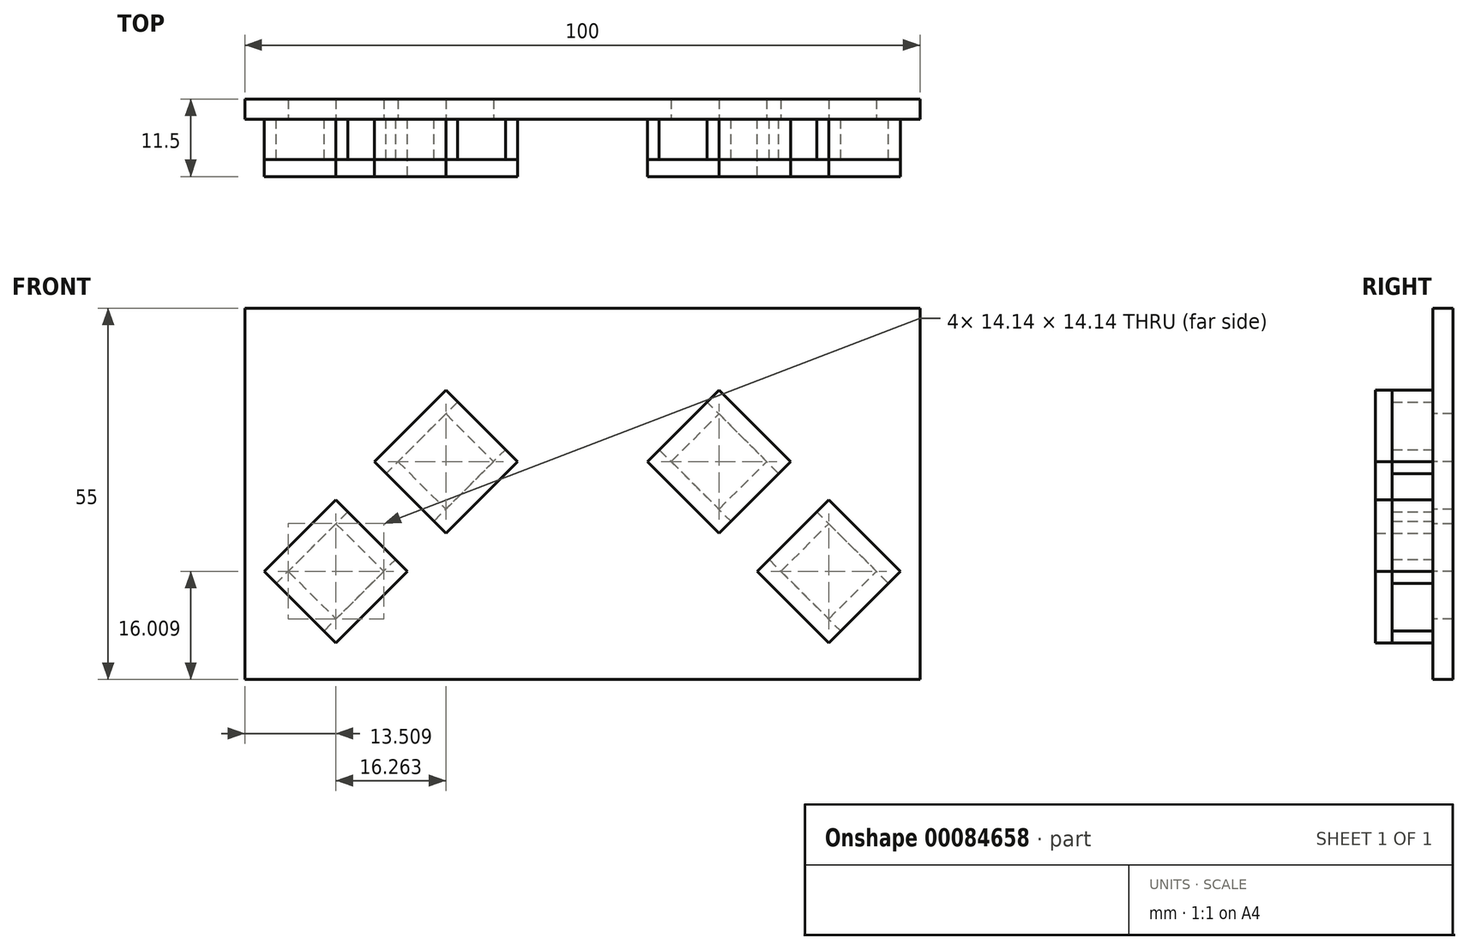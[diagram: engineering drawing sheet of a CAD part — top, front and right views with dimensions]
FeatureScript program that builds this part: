
annotation { "Feature Type Name" : "Feature", "Feature Type Description" : "" }
export const myFeature = defineFeature(function(context is Context, id is Id, definition is map)
    precondition{}
    {
        {
            var Q0;
            Q0=qCreatedBy(makeId("Front.planeOp"),FACE);
            var sketch = newSketch(context, id + "F0", { "sketchPlane" : qUnion([Q0])});
            skLineSegment(sketch, "E0.top", {"start": v(50, -45) * mm, "end": v(-50, -45) * mm});
            skLineSegment(sketch, "E0.left", {"start": v(50, 0) * mm, "end": v(50, -45) * mm});
            skLineSegment(sketch, "E0.right", {"start": v(-50, 0) * mm, "end": v(-50, -45) * mm});
            skPoint(sketch, "E0.middle", {"position": v(0, 0) * mm});
            skLineSegment(sketch, "E1", {"start": v(0, 0) * mm, "end": v(0, -45) * mm});
            skLineSegment(sketch, "E2", {"start": v(-50, 0) * mm, "end": v(50, 0) * mm});
            skLineSegment(sketch, "E3.0", {"start": v(13.16, -12.73) * mm, "end": v(20.23, -19.8) * mm});
            skLineSegment(sketch, "E4.0", {"start": v(20.23, -5.66) * mm, "end": v(27.3, -12.73) * mm});
            skLineSegment(sketch, "E5.0", {"start": v(-20.23, -5.66) * mm, "end": v(-13.16, -12.73) * mm});
            skLineSegment(sketch, "E6.0", {"start": v(13.16, -12.73) * mm, "end": v(20.23, -5.66) * mm});
            skLineSegment(sketch, "E7.0", {"start": v(-27.3, -12.73) * mm, "end": v(-20.23, -19.8) * mm});
            skLineSegment(sketch, "E8.0", {"start": v(20.23, -19.8) * mm, "end": v(27.3, -12.73) * mm});
            skLineSegment(sketch, "E9.0", {"start": v(-36.5, -21.92) * mm, "end": v(-29.42, -29) * mm});
            skLineSegment(sketch, "E10.0", {"start": v(29.42, -29) * mm, "end": v(36.5, -21.92) * mm});
            skLineSegment(sketch, "E11.0", {"start": v(-43.56, -29) * mm, "end": v(-36.5, -36.06) * mm});
            skLineSegment(sketch, "E12.0", {"start": v(36.5, -36.06) * mm, "end": v(43.56, -29) * mm});
            skLineSegment(sketch, "E13.trimOffspring", {"start": v(-36.5, -21.92) * mm, "end": v(-43.56, -29) * mm});
            skLineSegment(sketch, "E14.trimOffspring", {"start": v(-29.42, -29) * mm, "end": v(-36.5, -36.06) * mm});
            skLineSegment(sketch, "E15.trimOffspring", {"start": v(-20.23, -5.66) * mm, "end": v(-27.3, -12.73) * mm});
            skLineSegment(sketch, "E16.trimOffspring", {"start": v(-13.16, -12.73) * mm, "end": v(-20.23, -19.8) * mm});
            skLineSegment(sketch, "E17.trimOffspring", {"start": v(36.5, -21.92) * mm, "end": v(43.56, -29) * mm});
            skLineSegment(sketch, "E18.trimOffspring", {"start": v(29.42, -29) * mm, "end": v(36.5, -36.06) * mm});
            skPoint(sketch, "E19.start.orphan", {"position": v(44.27, -36.77) * mm});
            skLineSegment(sketch, "E20.top", {"start": v(-50, -45) * mm, "end": v(50, -45) * mm});
            skPoint(sketch, "E21.orphan", {"position": v(-50, 45) * mm});
            skPoint(sketch, "E0.bottom.end.orphan", {"position": v(0, 45) * mm});
            skPoint(sketch, "E22.orphan", {"position": v(50, 45) * mm});
            skLineSegment(sketch, "E23.0", {"start": v(-50, 10) * mm, "end": v(50, 10) * mm});
            skLineSegment(sketch, "E24", {"start": v(-50, 10) * mm, "end": v(-50, 0) * mm});
            skLineSegment(sketch, "E25", {"start": v(50, 10) * mm, "end": v(50, 0) * mm});
            skLineSegment(sketch, "E26", {"start": v(89.35, -24.6) * mm, "end": v(87.98, -26.52) * mm});
            skSolve(sketch);
        }
        {
            var Q0;
            Q0=makeQuery(id+"F0.imprint","IMPRINT",FACE,{"disambiguationData":[TD([[makeQuery(id+"F0.imprint","IMPRINT",EDGE,{"derivedFrom":sQuery(id+"F0.wireOp",EDGE,"E5.0")}),1.0]])]});
            var sketch = newSketch(context, id + "F1", { "sketchPlane" : qUnion([Q0])});
            skLineSegment(sketch, "E27.0", {"start": v(-20.23, -5.66) * mm, "end": v(-27.3, -12.73) * mm});
            skLineSegment(sketch, "E28.0", {"start": v(-13.16, -12.73) * mm, "end": v(-20.23, -19.8) * mm});
            skLineSegment(sketch, "E29.0", {"start": v(-36.5, -21.92) * mm, "end": v(-43.56, -29) * mm});
            skLineSegment(sketch, "E30.0", {"start": v(-29.42, -29) * mm, "end": v(-36.5, -36.06) * mm});
            skLineSegment(sketch, "E31.0", {"start": v(-20.23, -2.12) * mm, "end": v(-18.46, -3.89) * mm});
            skLineSegment(sketch, "E31.1", {"start": v(-20.23, -2.12) * mm, "end": v(-30.83, -12.73) * mm});
            skLineSegment(sketch, "E31.2", {"start": v(-30.83, -12.73) * mm, "end": v(-29.07, -14.5) * mm});
            skLineSegment(sketch, "E31.3", {"start": v(-9.62, -12.73) * mm, "end": v(-20.23, -23.33) * mm});
            skLineSegment(sketch, "E32.0", {"start": v(-36.5, -18.38) * mm, "end": v(-34.72, -20.15) * mm});
            skLineSegment(sketch, "E32.1", {"start": v(-36.5, -18.38) * mm, "end": v(-47.1, -29) * mm});
            skLineSegment(sketch, "E32.2", {"start": v(-47.1, -29) * mm, "end": v(-45.33, -30.76) * mm});
            skLineSegment(sketch, "E32.3", {"start": v(-25.88, -29) * mm, "end": v(-36.5, -39.6) * mm});
            skLineSegment(sketch, "E33", {"start": v(-43.56, -29) * mm, "end": v(-45.33, -30.76) * mm});
            skLineSegment(sketch, "E34", {"start": v(-45.33, -30.76) * mm, "end": v(-36.5, -21.92) * mm});
            skLineSegment(sketch, "E35", {"start": v(-36.5, -21.92) * mm, "end": v(-34.72, -20.15) * mm});
            skLineSegment(sketch, "E36", {"start": v(-36.5, -36.06) * mm, "end": v(-38.26, -37.83) * mm});
            skLineSegment(sketch, "E37", {"start": v(-29.42, -29) * mm, "end": v(-27.65, -27.22) * mm});
            skLineSegment(sketch, "E38", {"start": v(-20.23, -19.8) * mm, "end": v(-22, -21.57) * mm});
            skLineSegment(sketch, "E39", {"start": v(-13.16, -12.73) * mm, "end": v(-11.39, -10.96) * mm});
            skLineSegment(sketch, "E40", {"start": v(-20.23, -5.66) * mm, "end": v(-18.46, -3.89) * mm});
            skLineSegment(sketch, "E41", {"start": v(-27.3, -12.73) * mm, "end": v(-29.07, -14.5) * mm});
            skLineSegment(sketch, "E42.MirrorCS", {"start": v(43.56, -29) * mm, "end": v(45.33, -30.76) * mm});
            skLineSegment(sketch, "E43.MirrorCS", {"start": v(36.5, -36.06) * mm, "end": v(38.26, -37.83) * mm});
            skLineSegment(sketch, "E44.MirrorCS", {"start": v(36.5, -21.92) * mm, "end": v(34.72, -20.15) * mm});
            skLineSegment(sketch, "E45.MirrorCS", {"start": v(13.16, -12.73) * mm, "end": v(11.39, -10.96) * mm});
            skLineSegment(sketch, "E46.MirrorCS", {"start": v(29.42, -29) * mm, "end": v(27.65, -27.22) * mm});
            skLineSegment(sketch, "E47.MirrorCS", {"start": v(20.23, -5.66) * mm, "end": v(18.46, -3.89) * mm});
            skLineSegment(sketch, "E48.MirrorCS", {"start": v(20.23, -19.8) * mm, "end": v(22, -21.57) * mm});
            skLineSegment(sketch, "E49.MirrorCS", {"start": v(36.5, -21.92) * mm, "end": v(43.56, -29) * mm});
            skLineSegment(sketch, "E50.MirrorCS", {"start": v(27.3, -12.73) * mm, "end": v(29.07, -14.5) * mm});
            skLineSegment(sketch, "E51.MirrorCS", {"start": v(47.1, -29) * mm, "end": v(45.33, -30.76) * mm});
            skLineSegment(sketch, "E52.MirrorCS", {"start": v(25.88, -29) * mm, "end": v(36.5, -39.6) * mm});
            skLineSegment(sketch, "E53.MirrorCS", {"start": v(36.5, -18.38) * mm, "end": v(47.1, -29) * mm});
            skLineSegment(sketch, "E54.MirrorCS", {"start": v(20.23, -5.66) * mm, "end": v(27.3, -12.73) * mm});
            skLineSegment(sketch, "E55.MirrorCS", {"start": v(13.16, -12.73) * mm, "end": v(20.23, -19.8) * mm});
            skLineSegment(sketch, "E56.MirrorCS", {"start": v(29.42, -29) * mm, "end": v(36.5, -36.06) * mm});
            skLineSegment(sketch, "E57.MirrorCS", {"start": v(45.33, -30.76) * mm, "end": v(36.5, -21.92) * mm});
            skLineSegment(sketch, "E58.MirrorCS", {"start": v(36.5, -18.38) * mm, "end": v(34.72, -20.15) * mm});
            skLineSegment(sketch, "E59.MirrorCS", {"start": v(20.23, -2.12) * mm, "end": v(30.83, -12.73) * mm});
            skLineSegment(sketch, "E60.MirrorCS", {"start": v(9.62, -12.73) * mm, "end": v(20.23, -23.33) * mm});
            skLineSegment(sketch, "E61.MirrorCS", {"start": v(20.23, -2.12) * mm, "end": v(18.46, -3.89) * mm});
            skLineSegment(sketch, "E62.MirrorCS", {"start": v(30.83, -12.73) * mm, "end": v(29.07, -14.5) * mm});
            skPoint(sketch, "E63.0.end.orphan", {"position": v(-13.16, -12.73) * mm});
            skPoint(sketch, "E63.0.start.orphan", {"position": v(-20.23, -5.66) * mm});
            skLineSegment(sketch, "E64.trimOffspring", {"start": v(-11.39, -10.96) * mm, "end": v(-9.62, -12.73) * mm});
            skPoint(sketch, "E65.0.start.orphan", {"position": v(-27.3, -12.73) * mm});
            skLineSegment(sketch, "E66.trimOffspring", {"start": v(-22, -21.57) * mm, "end": v(-20.23, -23.33) * mm});
            skLineSegment(sketch, "E67.trimOffspring", {"start": v(-27.65, -27.22) * mm, "end": v(-25.88, -29) * mm});
            skPoint(sketch, "E68.0.start.orphan", {"position": v(-43.56, -29) * mm});
            skLineSegment(sketch, "E69.trimOffspring", {"start": v(-38.26, -37.83) * mm, "end": v(-36.5, -39.6) * mm});
            skLineSegment(sketch, "E70.trimOffspring", {"start": v(11.39, -10.96) * mm, "end": v(9.62, -12.73) * mm});
            skPoint(sketch, "E71.MirrorCS.end.orphan", {"position": v(13.16, -12.73) * mm});
            skPoint(sketch, "E71.MirrorCS.start.orphan", {"position": v(20.23, -5.66) * mm});
            skPoint(sketch, "E72.MirrorCS.start.orphan", {"position": v(27.3, -12.73) * mm});
            skLineSegment(sketch, "E73.trimOffspring", {"start": v(22, -21.57) * mm, "end": v(20.23, -23.33) * mm});
            skLineSegment(sketch, "E74.trimOffspring", {"start": v(27.65, -27.22) * mm, "end": v(25.88, -29) * mm});
            skPoint(sketch, "E75.MirrorCS.start.orphan", {"position": v(43.56, -29) * mm});
            skLineSegment(sketch, "E76.trimOffspring", {"start": v(38.26, -37.83) * mm, "end": v(36.5, -39.6) * mm});
            skSolve(sketch);
        }
        {
            var Q0;
            Q0 = qSketchRegion(id + "F1", true);
            extrude(context, id + "F2", {"entities" : qUnion([Q0]), "depth" : 6 * mm});
        }
        {
            var Q0;
            Q0=makeQuery(id+"F2.opExtrude","CAP_FACE",FACE,{"disambiguationData":[OSD([sQuery(id+"F1.wireOp",EDGE,"E27.0"),sQuery(id+"F1.wireOp",EDGE,"E31.0"),sQuery(id+"F1.wireOp",EDGE,"E31.1"),sQuery(id+"F1.wireOp",EDGE,"E31.2"),sQuery(id+"F1.wireOp",EDGE,"E40"),sQuery(id+"F1.wireOp",EDGE,"E41")])],"isStart":false});
            var sketch = newSketch(context, id + "F3", { "sketchPlane" : qUnion([Q0])});
            skLineSegment(sketch, "E77.0", {"start": v(-36.5, -18.38) * mm, "end": v(-47.1, -29) * mm});
            skLineSegment(sketch, "E78.0", {"start": v(-25.88, -29) * mm, "end": v(-36.5, -39.6) * mm});
            skLineSegment(sketch, "E79.0", {"start": v(-20.23, -2.12) * mm, "end": v(-30.83, -12.73) * mm});
            skLineSegment(sketch, "E80.0", {"start": v(-9.62, -12.73) * mm, "end": v(-20.23, -23.33) * mm});
            skLineSegment(sketch, "E81.0.0", {"start": v(0, -45) * mm, "end": v(50, -45) * mm});
            skLineSegment(sketch, "E81.0.1", {"start": v(50, -45) * mm, "end": v(50, 0) * mm});
            skLineSegment(sketch, "E81.0.2", {"start": v(50, 0) * mm, "end": v(0, 0) * mm});
            skLineSegment(sketch, "E81.0.3", {"start": v(0, 0) * mm, "end": v(0, -45) * mm});
            skLineSegment(sketch, "E82.0", {"start": v(9.62, -12.73) * mm, "end": v(20.23, -23.33) * mm});
            skLineSegment(sketch, "E83.0", {"start": v(36.5, -18.38) * mm, "end": v(47.1, -29) * mm});
            skLineSegment(sketch, "E84.0", {"start": v(25.88, -29) * mm, "end": v(36.5, -39.6) * mm});
            skLineSegment(sketch, "E85", {"start": v(-36.5, -18.38) * mm, "end": v(-25.88, -29) * mm});
            skLineSegment(sketch, "E86", {"start": v(-47.1, -29) * mm, "end": v(-36.5, -39.6) * mm});
            skLineSegment(sketch, "E87", {"start": v(-30.83, -12.73) * mm, "end": v(-20.23, -23.33) * mm});
            skLineSegment(sketch, "E88", {"start": v(-20.23, -2.12) * mm, "end": v(-9.62, -12.73) * mm});
            skLineSegment(sketch, "E89.0", {"start": v(20.23, -2.12) * mm, "end": v(30.83, -12.73) * mm});
            skLineSegment(sketch, "E90", {"start": v(20.23, -2.12) * mm, "end": v(9.62, -12.73) * mm});
            skLineSegment(sketch, "E91", {"start": v(30.83, -12.73) * mm, "end": v(20.23, -23.33) * mm});
            skLineSegment(sketch, "E92", {"start": v(36.5, -18.38) * mm, "end": v(25.88, -29) * mm});
            skLineSegment(sketch, "E93", {"start": v(47.1, -29) * mm, "end": v(36.5, -39.6) * mm});
            skSolve(sketch);
        }
        {
            var Q0;
            Q0=makeQuery(id+"F3.imprint","IMPRINT",FACE,{"disambiguationData":[TD([[makeQuery(id+"F3.imprint","IMPRINT",EDGE,{"derivedFrom":sQuery(id+"F3.wireOp",EDGE,"E77.0")}),1.0]])]});
            var Q1;
            {var subQ0=sQuery(id+"F3.wireOp",EDGE,"E79.0");Q1=makeQuery(id+"F3.imprint","IMPRINT",FACE,{"disambiguationData":[TD([[makeQuery(id+"F3.imprint","IMPRINT",EDGE,{"derivedFrom":subQ0}),1.0]])]});}
            var Q2;
            {var subQ0=sQuery(id+"F3.wireOp",EDGE,"E80.0");Q2=makeQuery(id+"F3.imprint","IMPRINT",FACE,{"disambiguationData":[TD([[makeQuery(id+"F3.imprint","IMPRINT",EDGE,{"derivedFrom":subQ0}),-1.0]])]});}
            var Q3;
            Q3=makeQuery(id+"F3.imprint","IMPRINT",FACE,{"disambiguationData":[TD([[makeQuery(id+"F3.imprint","IMPRINT",EDGE,{"derivedFrom":sQuery(id+"F3.wireOp",EDGE,"E82.0")}),1.0]])]});
            var Q4;
            Q4=makeQuery(id+"F3.imprint","IMPRINT",FACE,{"disambiguationData":[TD([[makeQuery(id+"F3.imprint","IMPRINT",EDGE,{"derivedFrom":sQuery(id+"F3.wireOp",EDGE,"E83.0")}),-1.0]])]});
            extrude(context, id + "F4", {"entities" : qUnion([Q0, Q1, Q2, Q3, Q4]), "depth" : 2.5 * mm});
        }
        {
            var Q0;
            Q0=makeQuery(id+"F0.imprint","IMPRINT",FACE,{"disambiguationData":[TD([[makeQuery(id+"F0.imprint","IMPRINT",EDGE,{"derivedFrom":sQuery(id+"F0.wireOp",EDGE,"E23.0")}),-1.0]])]});
            var Q1;
            {var subQ1=sQuery(id+"F0.wireOp",EDGE,"E1");Q1=makeQuery(id+"F0.imprint","IMPRINT",FACE,{"disambiguationData":[TD([[makeQuery(id+"F0.imprint","IMPRINT",EDGE,{"derivedFrom":subQ1}),1.0]])]});}
            var Q2;
            {var subQ1=sQuery(id+"F0.wireOp",EDGE,"E1");Q2=makeQuery(id+"F0.imprint","IMPRINT",FACE,{"disambiguationData":[TD([[makeQuery(id+"F0.imprint","IMPRINT",EDGE,{"derivedFrom":subQ1}),-1.0]])]});}
            extrude(context, id + "F5", {"entities" : qUnion([Q0, Q1, Q2]), "oppositeDirection" : true, "depth" : 3 * mm});
        }
    });
